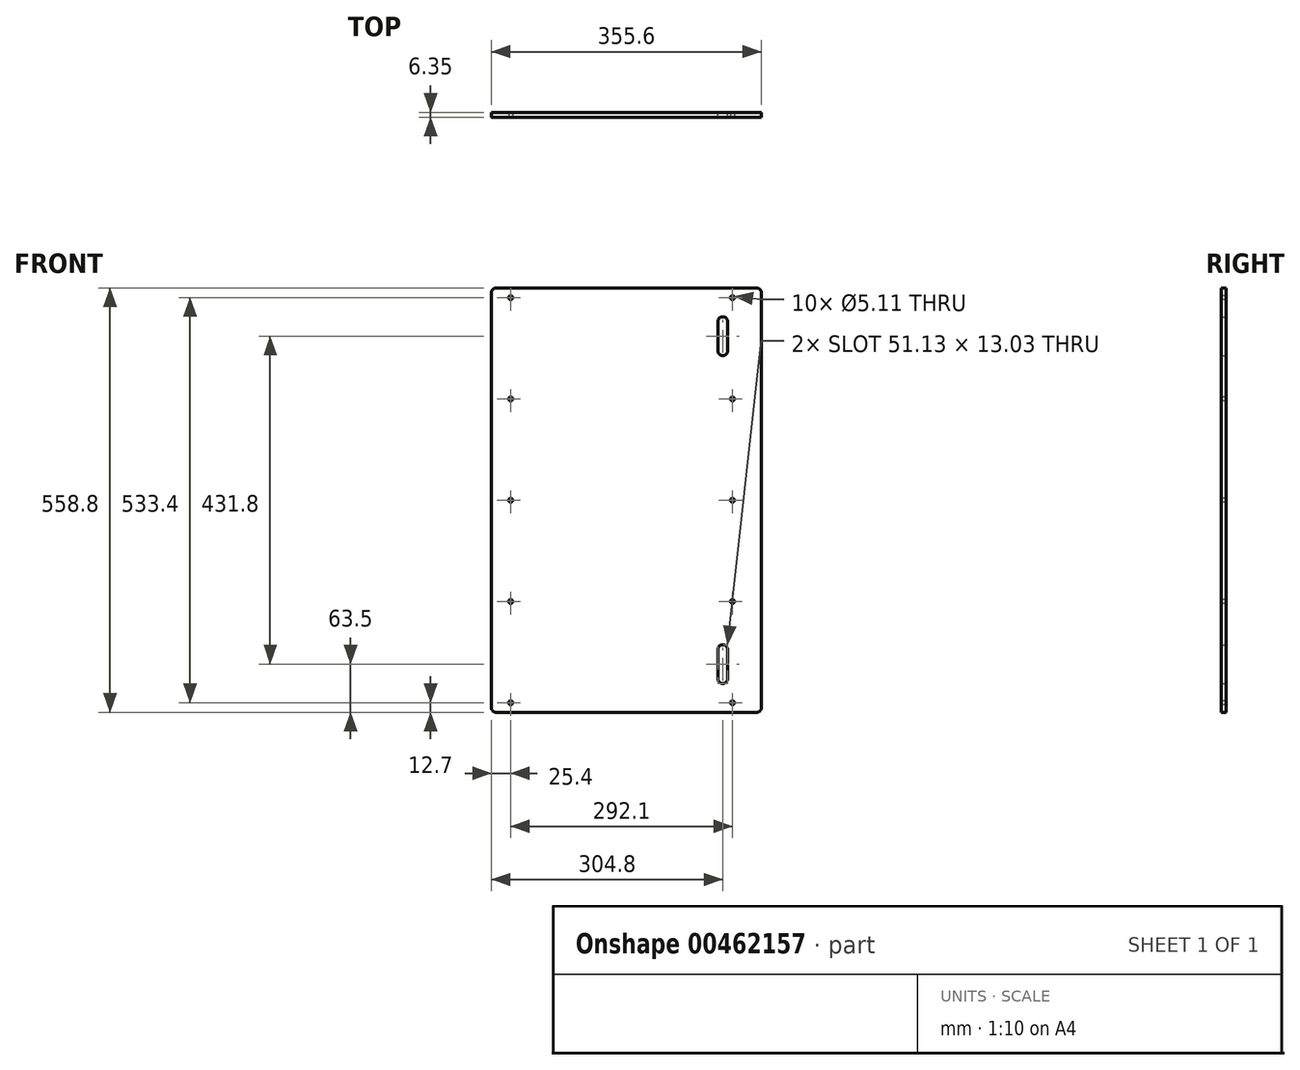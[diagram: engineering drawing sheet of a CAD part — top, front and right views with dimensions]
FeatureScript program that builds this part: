
annotation { "Feature Type Name" : "Feature", "Feature Type Description" : "" }
export const myFeature = defineFeature(function(context is Context, id is Id, definition is map)
    precondition{}
    {
        {
            var Q0;
            Q0=qCreatedBy(makeId("Front.planeOp"),FACE);
            var sketch = newSketch(context, id + "F0", { "sketchPlane" : qUnion([Q0])});
            skLineSegment(sketch, "E0.bottom", {"start": v(171.45, -279.4) * mm, "end": v(-171.45, -279.4) * mm});
            skLineSegment(sketch, "E0.top", {"start": v(171.45, 279.4) * mm, "end": v(-171.45, 279.4) * mm});
            skLineSegment(sketch, "E0.left", {"start": v(177.8, -273.05) * mm, "end": v(177.8, 273.05) * mm});
            skLineSegment(sketch, "E0.right", {"start": v(-177.8, -273.05) * mm, "end": v(-177.8, 273.05) * mm});
            skPoint(sketch, "E0.middle", {"position": v(0, 0) * mm});
            skPoint(sketch, "E1.visualSharp", {"position": v(177.8, 279.4) * mm});
            skArc(sketch, "E1.filletArc", {"start": v(177.8, 273.05) * mm, "mid": v(175.94, 277.54) * mm, "end": v(171.45, 279.4) * mm});
            skPoint(sketch, "E2.visualSharp", {"position": v(-177.8, 279.4) * mm});
            skArc(sketch, "E2.filletArc", {"start": v(-171.45, 279.4) * mm, "mid": v(-175.94, 277.54) * mm, "end": v(-177.8, 273.05) * mm});
            skPoint(sketch, "E3.visualSharp", {"position": v(-177.8, -279.4) * mm});
            skArc(sketch, "E3.filletArc", {"start": v(-177.8, -273.05) * mm, "mid": v(-175.94, -277.54) * mm, "end": v(-171.45, -279.4) * mm});
            skPoint(sketch, "E4.visualSharp", {"position": v(177.8, -279.4) * mm});
            skArc(sketch, "E4.filletArc", {"start": v(171.45, -279.4) * mm, "mid": v(175.94, -277.54) * mm, "end": v(177.8, -273.05) * mm});
            skLineSegment(sketch, "E5", {"start": v(-152.4, 279.4) * mm, "end": v(-152.4, -279.4) * mm, "construction": true});
            skLineSegment(sketch, "E6", {"start": v(139.7, 279.4) * mm, "end": v(139.7, -279.4) * mm, "construction": true});
            skPoint(sketch, "E7", {"position": v(-152.4, -266.7) * mm});
            skPoint(sketch, "E8", {"position": v(-152.4, -133.35) * mm});
            skPoint(sketch, "E9", {"position": v(-152.4, 0) * mm});
            skPoint(sketch, "E10", {"position": v(-152.4, 133.35) * mm});
            skPoint(sketch, "E11", {"position": v(-152.4, 266.7) * mm});
            skPoint(sketch, "E12", {"position": v(139.7, 266.7) * mm});
            skPoint(sketch, "E13", {"position": v(139.7, 133.35) * mm});
            skPoint(sketch, "E14", {"position": v(139.7, 0) * mm});
            skPoint(sketch, "E15", {"position": v(139.7, -133.35) * mm});
            skPoint(sketch, "E16", {"position": v(139.7, -266.7) * mm});
            skLineSegment(sketch, "E17", {"start": v(127, -196.85) * mm, "end": v(127, -234.95) * mm, "construction": true});
            skPoint(sketch, "E18", {"position": v(127, -215.9) * mm});
            skArc(sketch, "E19.0.startCap", {"start": v(133.52, -234.95) * mm, "mid": v(127, -241.47) * mm, "end": v(120.48, -234.95) * mm});
            skArc(sketch, "E19.0.endCap", {"start": v(120.48, -196.85) * mm, "mid": v(127, -190.33) * mm, "end": v(133.52, -196.85) * mm});
            skLineSegment(sketch, "E19.0.left", {"start": v(120.48, -196.85) * mm, "end": v(120.48, -234.95) * mm});
            skLineSegment(sketch, "E19.0.right", {"start": v(133.52, -196.85) * mm, "end": v(133.52, -234.95) * mm});
            skArc(sketch, "E20.MirrorCS", {"start": v(133.52, 234.95) * mm, "mid": v(127, 241.47) * mm, "end": v(120.48, 234.95) * mm});
            skLineSegment(sketch, "E21.MirrorCS", {"start": v(133.52, 196.85) * mm, "end": v(133.52, 234.95) * mm});
            skLineSegment(sketch, "E22.MirrorCS", {"start": v(120.48, 196.85) * mm, "end": v(120.48, 234.95) * mm});
            skArc(sketch, "E23.MirrorCS", {"start": v(120.48, 196.85) * mm, "mid": v(127, 190.33) * mm, "end": v(133.52, 196.85) * mm});
            skSolve(sketch);
        }
        {
            var Q0;
            Q0 = qSketchRegion(id + "F0", true);
            extrude(context, id + "F1", {"entities" : qUnion([Q0]), "depth" : 6.35 * mm});
        }
        {
            var Q0;
            Q0=sQuery(id+"F0.wireOp",VERTEX,"E16");
            var Q1;
            Q1=sQuery(id+"F0.wireOp",VERTEX,"E15");
            var Q2;
            Q2=sQuery(id+"F0.wireOp",VERTEX,"E14");
            var Q3;
            Q3=sQuery(id+"F0.wireOp",VERTEX,"E13");
            var Q4;
            Q4=sQuery(id+"F0.wireOp",VERTEX,"E12");
            var Q5;
            Q5=sQuery(id+"F0.wireOp",VERTEX,"E7");
            var Q6;
            Q6=sQuery(id+"F0.wireOp",VERTEX,"E9");
            var Q7;
            Q7=sQuery(id+"F0.wireOp",VERTEX,"E10");
            var Q8;
            Q8=sQuery(id+"F0.wireOp",VERTEX,"E11");
            var Q9;
            Q9=sQuery(id+"F0.wireOp",VERTEX,"E8");
            var Q10;
            Q10=makeQuery(id+"F1.opExtrude","SWEPT_BODY",BODY,{"disambiguationData":[OSD([sQuery(id+"F0.wireOp",EDGE,"E0.bottom"),sQuery(id+"F0.wireOp",EDGE,"E0.top"),sQuery(id+"F0.wireOp",EDGE,"E0.left"),sQuery(id+"F0.wireOp",EDGE,"E0.right"),sQuery(id+"F0.wireOp",EDGE,"E1.filletArc"),sQuery(id+"F0.wireOp",EDGE,"E2.filletArc"),sQuery(id+"F0.wireOp",EDGE,"E3.filletArc"),sQuery(id+"F0.wireOp",EDGE,"E4.filletArc"),sQuery(id+"F0.wireOp",EDGE,"E19.0.startCap"),sQuery(id+"F0.wireOp",EDGE,"E19.0.endCap"),sQuery(id+"F0.wireOp",EDGE,"E19.0.left"),sQuery(id+"F0.wireOp",EDGE,"E19.0.right"),sQuery(id+"F0.wireOp",EDGE,"E20.MirrorCS"),sQuery(id+"F0.wireOp",EDGE,"E21.MirrorCS"),sQuery(id+"F0.wireOp",EDGE,"E22.MirrorCS"),sQuery(id+"F0.wireOp",EDGE,"E23.MirrorCS")])]});
            hole(context, id + "F2", {"style" : HoleStyle.SIMPLE, "endStyle" : HoleEndStyle.THROUGH, "oppositeDirection" : true, "standardTappedOrClearance" : lookupTablePath({ "standard" : "ANSI", "engagement" : "75%", "pitch" : "20 tpi", "size" : "1/4", "type" : "Tapped" }), "standardBlindInLast" : lookupTablePath({ "standard" : "ANSI", "engagement" : "75%", "pitch" : "20 tpi", "size" : "1/4", "type" : "Tapped" }), "holeDiameter" : 5.1 * mm, "showTappedDepth" : true, "isTappedThrough" : true, "tappedDepth" : 57.15 * mm, "tapClearance" : 3, "locations" : qUnion([Q0, Q1, Q2, Q3, Q4, Q5, Q6, Q7, Q8, Q9]), "scope" : qUnion([Q10]), "majorDiameter" : 6.35 * mm, "startStyle" : HoleStartStyle.SKETCH});
        }
    });
